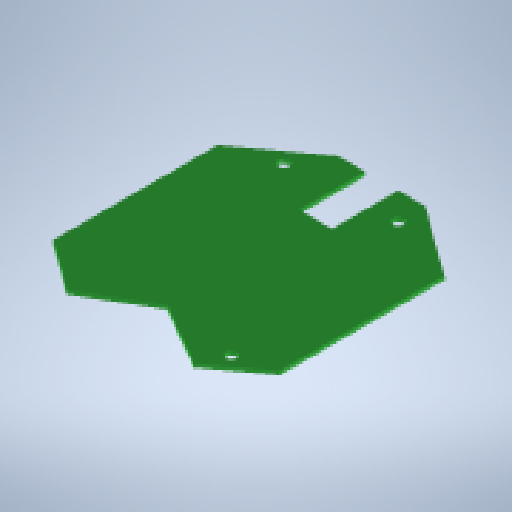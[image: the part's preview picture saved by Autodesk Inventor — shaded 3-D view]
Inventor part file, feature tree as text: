
AUTODESK INVENTOR PART (.ipt)
format: ipt  version: 2024 (Build 280153000, 153)  size: 286,720 bytes
history: native  units: in
note: dims shown in document units (in); Inventor stores cm internally (conversion verified against a paired STEP export)
features: extrude x1, sketch x1
ambient origin geometry x8: Origin, YZ Plane, XZ Plane, XY Plane, X Axis, Y Axis, Z Axis, Center Point
bodies: Solid1 (feature_tree)
feature tree (2):
  extrude  "Extrusion1"  Depth=0.5315in
  sketch  "Sketch1"  dims[d0=2.4803in d1=0.6299in d2=0.0984in d3=0.0669in d4=120.0deg d6=0.0984in d7=0.0669in d8=0.0098in d9=0.0315in d10=0.0in d11=0.2638in d12=0.5315in d13=0.0098in d15=0.0098in d16=0.0098in d24=0.2362in d25=0.0866in d26=0.2362in d27=0.0866in d28=0.2362in d29=0.0866in d30=0.2165in d31=0.2165in d32=0.3858in d33=0.2717in d36=0.2047in d37=0.3031in d38=0.1575in d39=0.1575in d40=0.1575in]
